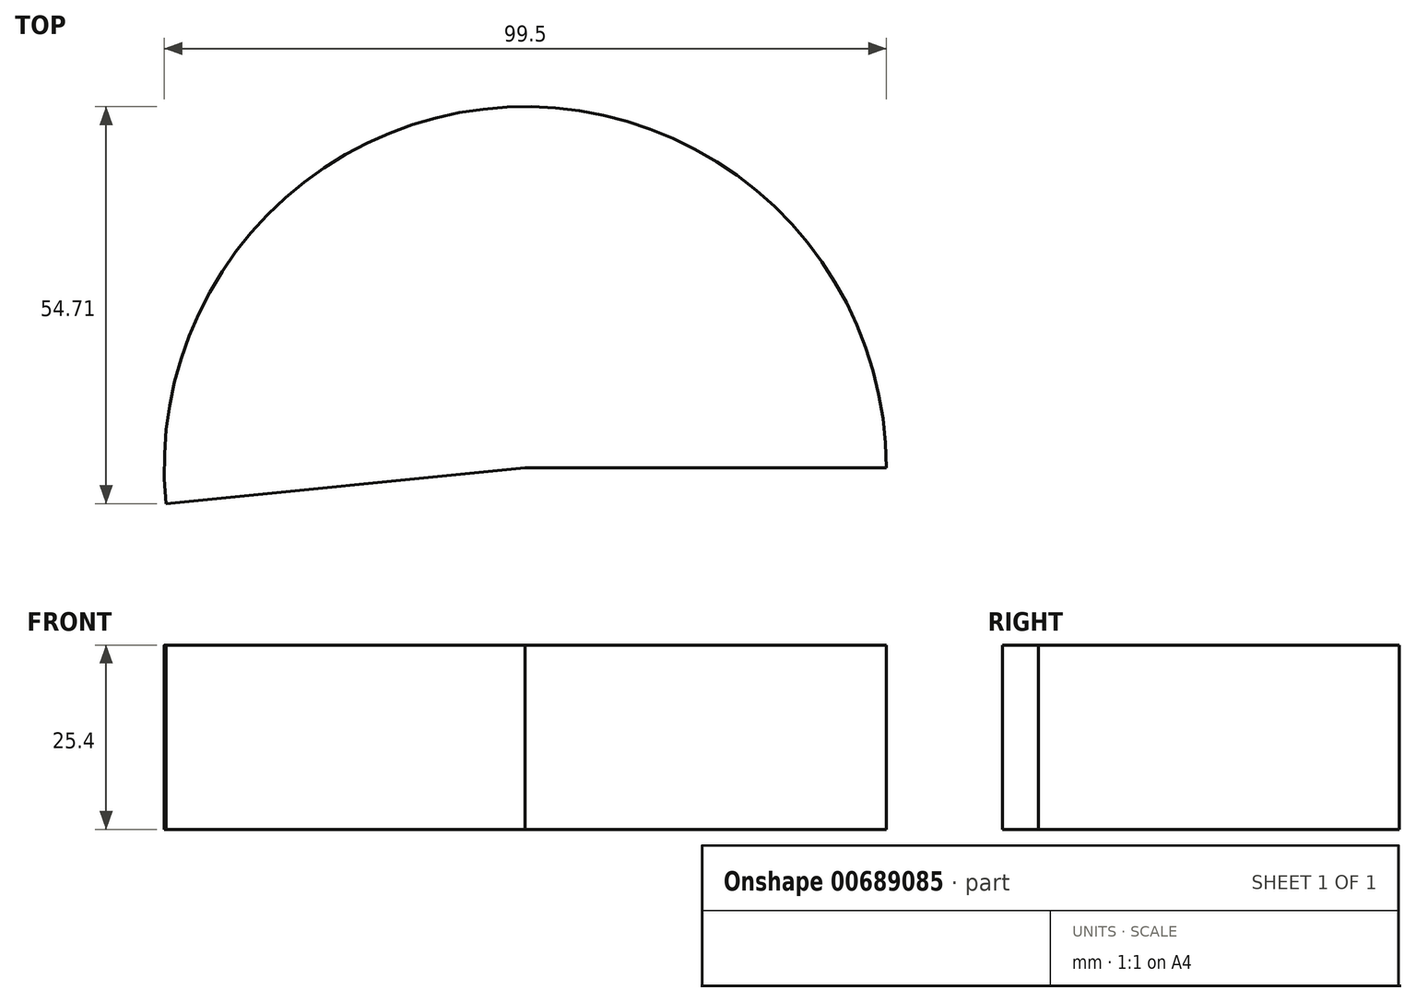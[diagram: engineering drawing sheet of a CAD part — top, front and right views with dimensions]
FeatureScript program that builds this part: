
annotation { "Feature Type Name" : "Feature", "Feature Type Description" : "" }
export const myFeature = defineFeature(function(context is Context, id is Id, definition is map)
    precondition{}
    {
        {
            var Q0;
            Q0=qCreatedBy(makeId("Top.planeOp"),FACE);
            var sketch = newSketch(context, id + "F0", { "sketchPlane" : qUnion([Q0])});
            skArc(sketch, "E0", {"start": v(49.75, 0) * mm, "mid": v(-2.48, 49.69) * mm, "end": v(-49.5, -4.96) * mm});
            skLineSegment(sketch, "E1", {"start": v(0, 0) * mm, "end": v(-49.5, -4.96) * mm});
            skLineSegment(sketch, "E2", {"start": v(0, 0) * mm, "end": v(49.75, 0) * mm});
            skSolve(sketch);
        }
        {
            var Q0;
            Q0=makeQuery(id+"F0.imprint","IMPRINT",FACE,{"disambiguationData":[TD([[makeQuery(id+"F0.imprint","IMPRINT",EDGE,{"derivedFrom":sQuery(id+"F0.wireOp",EDGE,"E0")}),1.0]])]});
            extrude(context, id + "F1", {"entities" : qUnion([Q0]), "depth" : 25.4 * mm, "offsetDistance" : 25.4 * mm});
        }
    });
